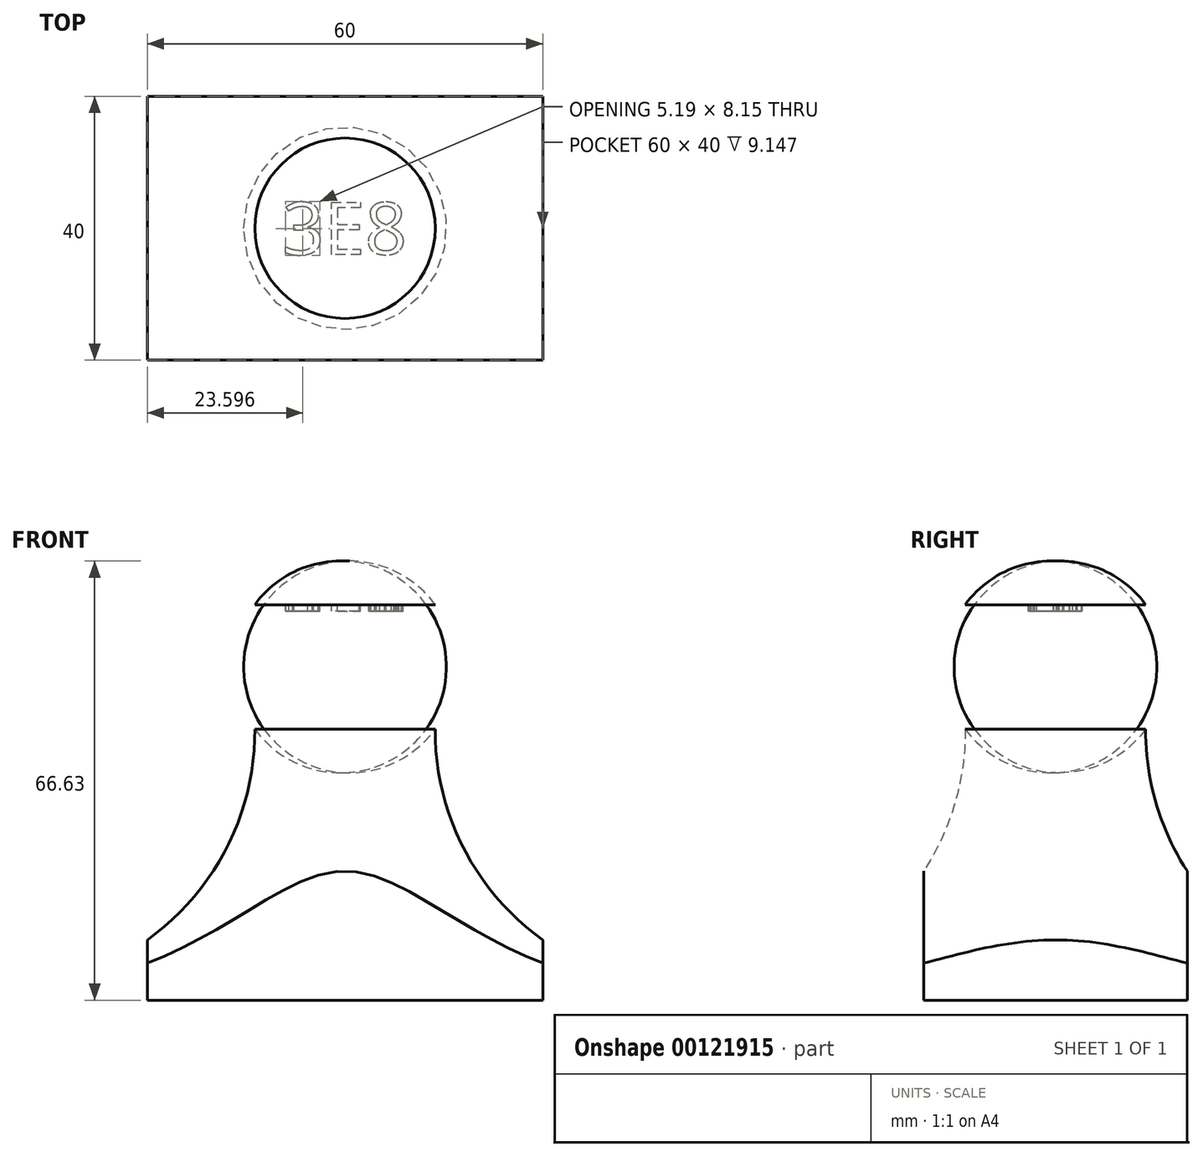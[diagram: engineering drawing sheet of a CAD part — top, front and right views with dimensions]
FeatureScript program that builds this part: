
annotation { "Feature Type Name" : "Feature", "Feature Type Description" : "" }
export const myFeature = defineFeature(function(context is Context, id is Id, definition is map)
    precondition{}
    {
        {
            var Q0;
            Q0=qCreatedBy(makeId("Front.planeOp"),FACE);
            var sketch = newSketch(context, id + "F0", { "sketchPlane" : qUnion([Q0])});
            skLineSegment(sketch, "E0", {"start": v(0, 0) * mm, "end": v(50, 0) * mm});
            skArc(sketch, "E1", {"start": v(13.7, 41.14) * mm, "mid": v(24.08, 14.36) * mm, "end": v(50, 2) * mm});
            skArc(sketch, "E2", {"start": v(13.7, 41.14) * mm, "mid": v(16.75, 50.57) * mm, "end": v(13.7, 60) * mm});
            skLineSegment(sketch, "E3", {"start": v(13.7, 60) * mm, "end": v(0, 60) * mm});
            skLineSegment(sketch, "E4", {"start": v(0, 60) * mm, "end": v(0, 0) * mm});
            skLineSegment(sketch, "E5", {"start": v(50, 0) * mm, "end": v(50, 2) * mm});
            skSolve(sketch);
        }
        {
            var Q0;
            Q0 = qSketchRegion(id + "F0", true);
            var Q1;
            Q1=sQuery(id+"F0.wireOp",EDGE,"E4");
            revolve(context, id + "F1", {"entities" : qUnion([Q0]), "axis" : qUnion([Q1]), "revolveType" : RevolveType.FULL});
        }
        {
            var Q0;
            Q0=makeQuery(id+"F1.opRevolve","SWEPT_FACE",FACE,{"disambiguationData":[OSD([sQuery(id+"F0.wireOp",EDGE,"E0")])]});
            var sketch = newSketch(context, id + "F2", { "sketchPlane" : qUnion([Q0])});
            skLineSegment(sketch, "E6.bottom", {"start": v(30, -20) * mm, "end": v(-30, -20) * mm});
            skLineSegment(sketch, "E6.top", {"start": v(30, 20) * mm, "end": v(-30, 20) * mm});
            skLineSegment(sketch, "E6.left", {"start": v(30, -20) * mm, "end": v(30, 20) * mm});
            skLineSegment(sketch, "E6.right", {"start": v(-30, -20) * mm, "end": v(-30, 20) * mm});
            skPoint(sketch, "E6.middle", {"position": v(0, 0) * mm});
            skCircle(sketch, "E7.0", {"center": v(0, 0) * mm, "radius": 50 * mm});
            skSolve(sketch);
        }
        {
            var Q0;
            Q0 = qSketchRegion(id + "F2", true);
            extrude(context, id + "F3", {"entities" : qUnion([Q0]), "operationType" : NewBodyOperationType.REMOVE, "endBound" : BoundingType.THROUGH_ALL, "oppositeDirection" : true, "depth" : 25 * mm});
        }
        {
            var Q0;
            Q0=makeQuery(id+"F1.opRevolve","SWEPT_FACE",FACE,{"disambiguationData":[OSD([sQuery(id+"F0.wireOp",EDGE,"E3")])]});
            var sketch = newSketch(context, id + "F4", { "sketchPlane" : qUnion([Q0])});
            skText(sketch, "E8", { "text": "3E8", "fontName": "OpenSans-Regular.ttf"});
            const initialGuessF4  = {"E8": [-0.00951, -0.004, 1, 0, 0.008]};
            skSetInitialGuess(sketch, initialGuessF4);
            skSolve(sketch);
        }
        {
            var Q0;
            Q0 = qSketchRegion(id + "F4", true);
            extrude(context, id + "F5", {"entities" : qUnion([Q0]), "operationType" : NewBodyOperationType.REMOVE, "oppositeDirection" : true, "depth" : 1 * mm});
        }
    });
